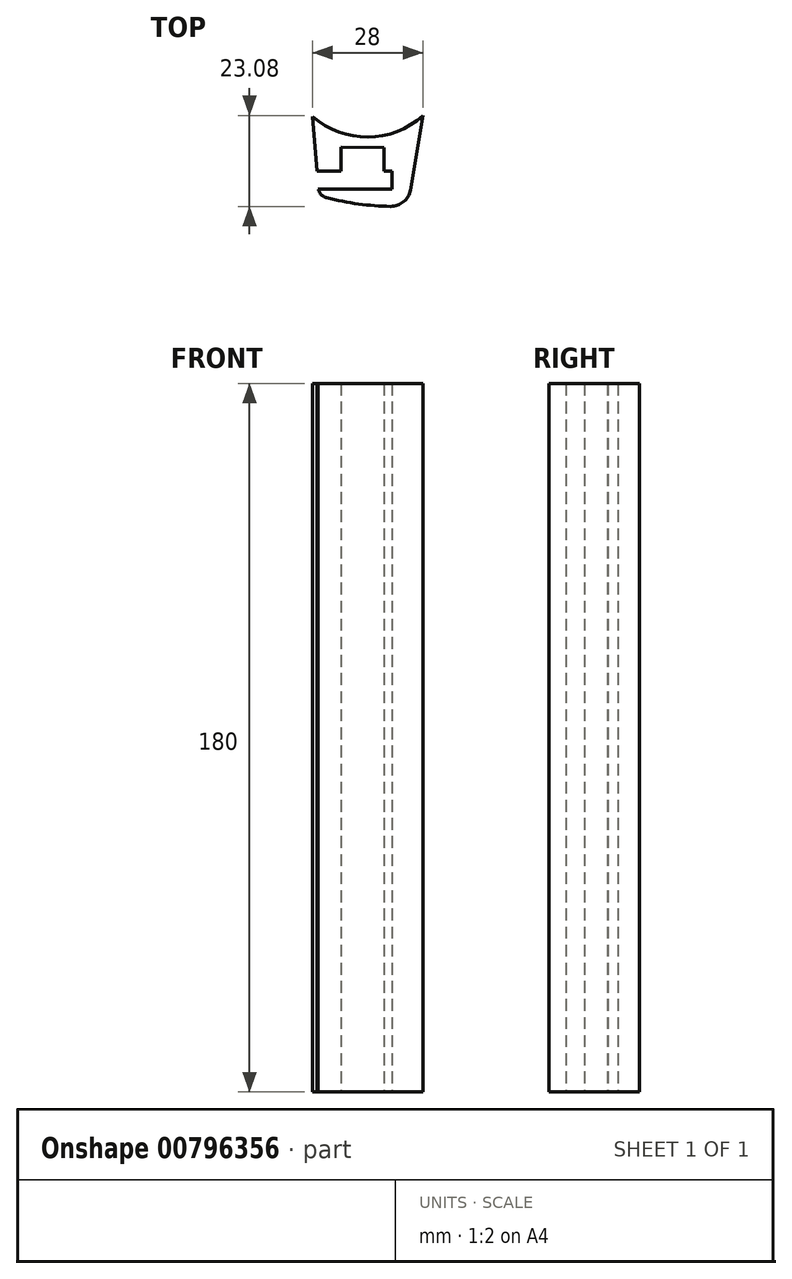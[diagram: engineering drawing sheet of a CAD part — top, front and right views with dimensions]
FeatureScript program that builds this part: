
annotation { "Feature Type Name" : "Feature", "Feature Type Description" : "" }
export const myFeature = defineFeature(function(context is Context, id is Id, definition is map)
    precondition{}
    {
        {
            var Q0;
            Q0=qCreatedBy(makeId("Top.planeOp"),FACE);
            var sketch = newSketch(context, id + "F0", { "sketchPlane" : qUnion([Q0])});
            skArc(sketch, "E0", {"start": v(-13.88, -15.76) * mm, "mid": v(0.16, -21) * mm, "end": v(14.12, -15.54) * mm});
            skLineSegment(sketch, "E1", {"start": v(-13.88, -15.76) * mm, "end": v(-12.71, -29.61) * mm});
            skLineSegment(sketch, "E2", {"start": v(14.12, -15.54) * mm, "end": v(10.28, -38.54) * mm});
            skLineSegment(sketch, "E3", {"start": v(-12.47, -35.79) * mm, "end": v(-12.47, -34.21) * mm});
            skLineSegment(sketch, "E4", {"start": v(-12.47, -34.21) * mm, "end": v(6.28, -34.21) * mm});
            skLineSegment(sketch, "E5", {"start": v(6.28, -34.21) * mm, "end": v(6.29, -29.61) * mm});
            skLineSegment(sketch, "E6", {"start": v(6.29, -29.61) * mm, "end": v(4.29, -29.6) * mm});
            skLineSegment(sketch, "E7", {"start": v(4.29, -29.6) * mm, "end": v(4.29, -23.66) * mm});
            skLineSegment(sketch, "E8", {"start": v(4.29, -23.66) * mm, "end": v(-6.71, -23.6) * mm});
            skLineSegment(sketch, "E9", {"start": v(-6.71, -23.6) * mm, "end": v(-6.71, -29.6) * mm});
            skLineSegment(sketch, "E10", {"start": v(-6.71, -29.6) * mm, "end": v(-12.71, -29.61) * mm});
            skArc(sketch, "E11", {"start": v(-12.47, -35.79) * mm, "mid": v(-1.22, -38.14) * mm, "end": v(10.28, -38.54) * mm});
            skSolve(sketch);
        }
        {
            var Q0;
            Q0=qSketchRegion(id+"F0",true);
            extrude(context, id + "F1", {"entities" : qUnion([Q0]), "depth" : 180 * mm, "offsetDistance" : 25 * mm});
        }
        {
            var Q0;
            Q0=makeQuery(id+"F1.opExtrude","SWEPT_EDGE",EDGE,{"disambiguationData":[OSD([sQuery(id+"F0.wireOp",EDGE,"E2"),sQuery(id+"F0.wireOp",EDGE,"E11")])]});
            fillet(context, id + "F2", {"entities" : qUnion([Q0]), "radius" : 5 * mm, "tangentPropagation" : true, "allowEdgeOverflow" : false});
        }
        {
            var Q0;
            Q0=makeQuery(id+"F1.opExtrude","SWEPT_EDGE",EDGE,{"disambiguationData":[OSD([sQuery(id+"F0.wireOp",EDGE,"E3"),sQuery(id+"F0.wireOp",EDGE,"E11")])]});
            fillet(context, id + "F3", {"entities" : qUnion([Q0]), "radius" : 3 * mm, "tangentPropagation" : true, "allowEdgeOverflow" : false});
        }
    });
